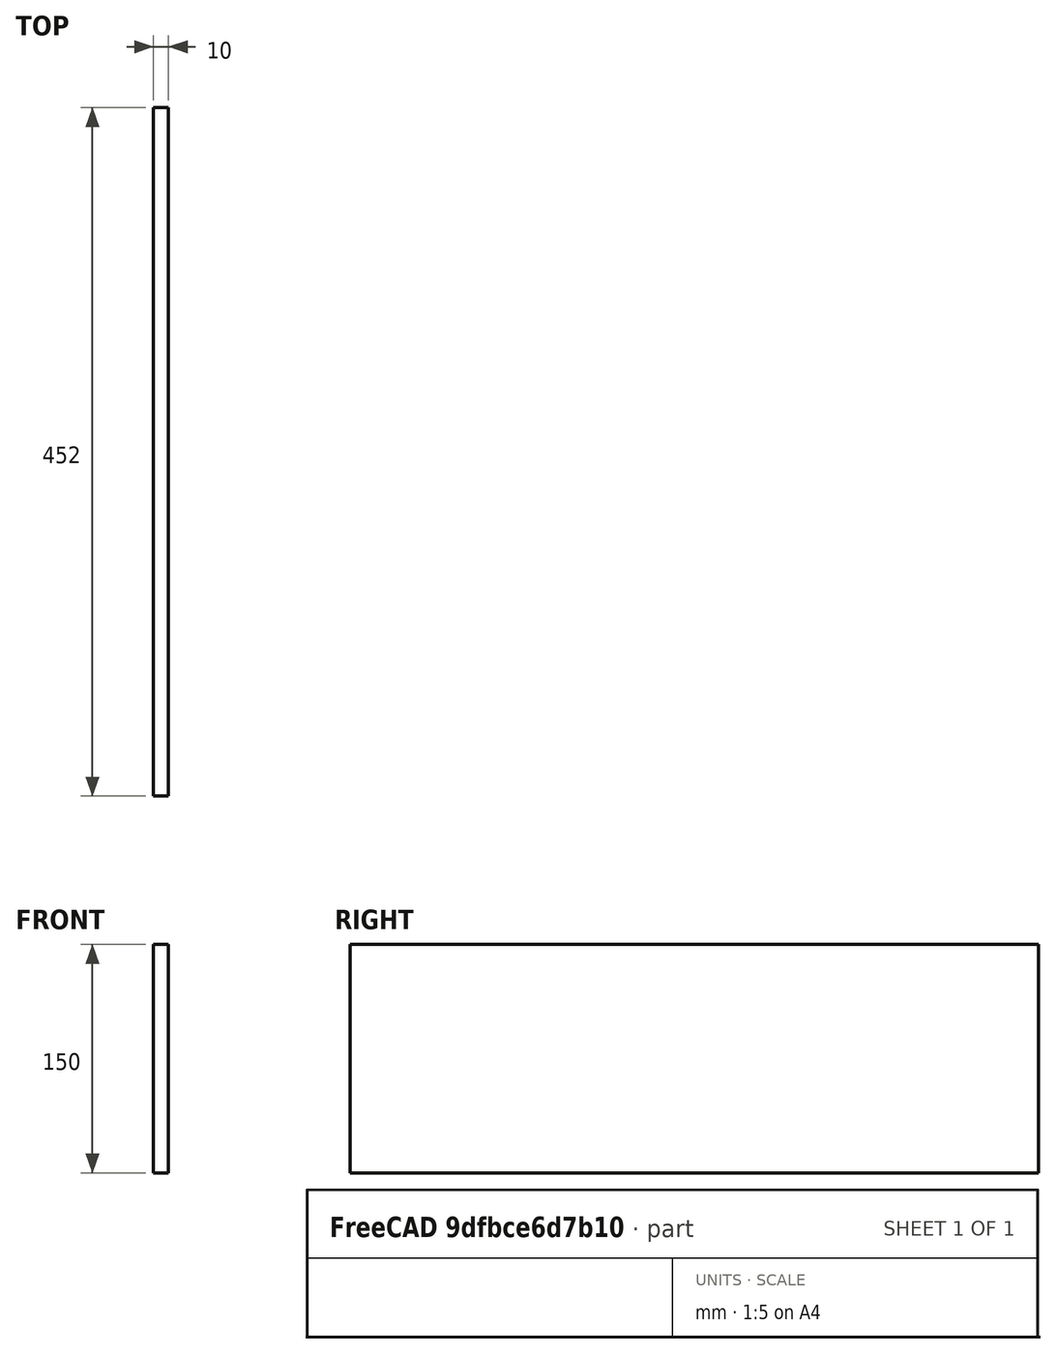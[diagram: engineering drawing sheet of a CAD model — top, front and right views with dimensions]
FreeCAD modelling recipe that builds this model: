
FCSTD DOCUMENT  (FreeCAD 0.18R16131 (Git))
Label: 500_Back_Horizontal_Mid
License: All rights reserved
LicenseURL: http://en.wikipedia.org/wiki/All_rights_reserved
objects: Sketcher::SketchObject×1, Spreadsheet::Sheet×1, PartDesign::Pad×1, PartDesign::Body×1
note: 4 computed .brp shape members not serialized (recipe doc carries the construction recipe); baked Part::Feature solids carry a one-line shape summary decoded from their .brp

FEATURE [Sketcher::SketchObject] Sketch
  MapMode = 4
  Placement = pos=(0,0,0) rot=(0.57735,0.57735,0.57735;2.0944rad)
  Support = -> [XY_Plane]
  expr: Constraints[6] = Spreadsheet.nY
  expr: Constraints[5] = Spreadsheet.nZ
  sketch-geometry (5):
    g0: LineSegment StartX=0 StartY=0 StartZ=0 EndX=0 EndY=150 EndZ=0
    g1: LineSegment StartX=452 StartY=0 StartZ=0 EndX=452 EndY=150 EndZ=0
    g2: LineSegment StartX=452 StartY=150 StartZ=0 EndX=0 EndY=150 EndZ=0
    g3: LineSegment StartX=226 StartY=0 StartZ=0 EndX=0 EndY=0 EndZ=0
    g4: LineSegment StartX=452 StartY=0 StartZ=0 EndX=226 EndY=0 EndZ=0
  constraints (14):
    c: Vertical(g0)
    c: Vertical(g1)
    c: Coincident(g2,g1)
    c: Coincident(g2,g0)
    c: Horizontal(g2)
    c: DistanceY(g1,g1) = 150
    c: DistanceX(g2,g2) = 452
    c: Coincident(g3,g0)
    c: Coincident(g4,g1)
    c: Horizontal(g4)
    c: Equal(g3,g4)
    c: Coincident(g4,g3)
    c: Horizontal(g3)
    c: Coincident(g0,g-1)
FEATURE [Spreadsheet::Sheet] Spreadsheet  label="xls"
  cells = B7=KEYBOARD FRONT; B8=Width; C8=nY; D8(nY)==500 - 19 - 19 - 10; B9=Height; C9=nZ; D9(nZ)=150; E9=F(T); B10=Thickness; C10=nT; D10(nT)=10
FEATURE [PartDesign::Pad] Pad
  Length = 10
  Length2 = 100
  Profile = -> Sketch
  Reversed = true
  Type = 0
  expr: Length = Spreadsheet.nT
FEATURE [PartDesign::Body] Body
  Group = -> [Sketch,Pad]
  Origin = -> Origin
  Tip = -> Pad
